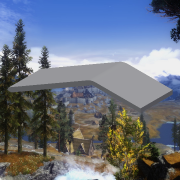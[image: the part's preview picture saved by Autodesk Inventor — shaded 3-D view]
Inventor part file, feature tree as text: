
AUTODESK INVENTOR PART (.ipt)
format: ipt  version: 2015 SP1 (Build 190203100, 203)  size: 168,448 bytes
history: native  units: in
note: dims shown in document units (in); Inventor stores cm internally (conversion verified against a paired STEP export)
features: sketch x2, extrude x1, hole x1, reference x1
ambient origin geometry x8: Origin, YZ Plane, XZ Plane, XY Plane, X Axis, Y Axis, Z Axis, Center Point
bodies: Solid1 (feature_tree)
feature tree (5):
  extrude  "Extrusion1"  TaperAngle=150.0deg  [1 undecoded]
  hole  "Hole1"  [1 undecoded]
  sketch  "Sketch1"  dims[d0=0.125in d1=150.0deg]
  sketch  "Sketch2"  dims[d2=2.915in d3=1.5in d5=0.125in d6=0.125in d7=0.125in d8=0.5in d9=1.0in d10=0.0in d11=0.163in d12=0.75in d13=0.375in d14=0.25in d15=0.5635in d16=1.0in d17=0.8108in]
  reference  "Reference1"
note: 2 required parameter values undecoded (feature->parameter linkage not recoverable at this tier; creation-order binding heuristic only, values carry confidence <= 0.55)
